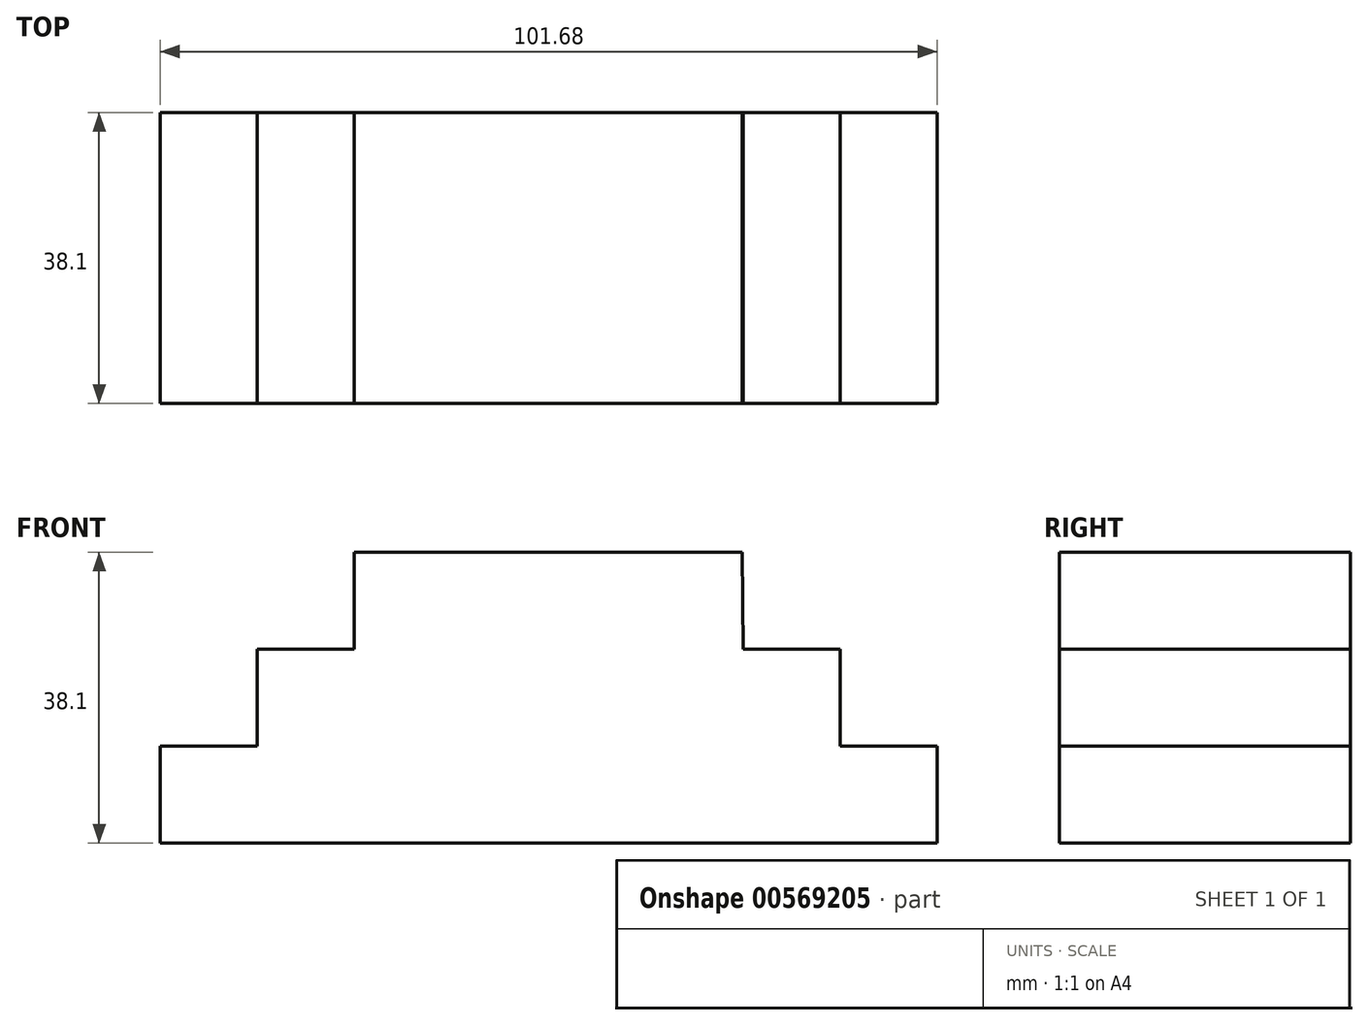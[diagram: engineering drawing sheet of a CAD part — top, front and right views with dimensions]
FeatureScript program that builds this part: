
annotation { "Feature Type Name" : "Feature", "Feature Type Description" : "" }
export const myFeature = defineFeature(function(context is Context, id is Id, definition is map)
    precondition{}
    {
        {
            var Q0;
            Q0=qCreatedBy(makeId("Front.planeOp"),FACE);
            var sketch = newSketch(context, id + "F0", { "sketchPlane" : qUnion([Q0])});
            skLineSegment(sketch, "E0", {"start": v(0, 0) * mm, "end": v(-50.8, 0) * mm});
            skLineSegment(sketch, "E1", {"start": v(-50.8, 0) * mm, "end": v(-50.8, -12.7) * mm});
            skLineSegment(sketch, "E2", {"start": v(-50.8, -12.7) * mm, "end": v(-63.5, -12.7) * mm});
            skLineSegment(sketch, "E3", {"start": v(-63.5, -12.7) * mm, "end": v(-63.5, -25.4) * mm});
            skLineSegment(sketch, "E4", {"start": v(-63.5, -25.4) * mm, "end": v(-76.2, -25.4) * mm});
            skLineSegment(sketch, "E5", {"start": v(-76.2, -25.4) * mm, "end": v(-76.2, -38.1) * mm});
            skLineSegment(sketch, "E6", {"start": v(-76.2, -38.1) * mm, "end": v(25.48, -38.1) * mm});
            skLineSegment(sketch, "E7", {"start": v(25.48, -38.1) * mm, "end": v(25.48, -25.4) * mm});
            skLineSegment(sketch, "E8", {"start": v(25.48, -25.4) * mm, "end": v(12.78, -25.4) * mm});
            skLineSegment(sketch, "E9", {"start": v(12.78, -25.4) * mm, "end": v(12.78, -12.7) * mm});
            skLineSegment(sketch, "E10", {"start": v(12.78, -12.7) * mm, "end": v(0.08, -12.7) * mm});
            skLineSegment(sketch, "E11", {"start": v(0.08, -12.7) * mm, "end": v(0, 0) * mm});
            skSolve(sketch);
        }
        {
            var Q0;
            Q0 = qSketchRegion(id + "F0", true);
            extrude(context, id + "F1", {"entities" : qUnion([Q0]), "depth" : 38.1 * mm, "offsetDistance" : 25.4 * mm});
        }
    });
